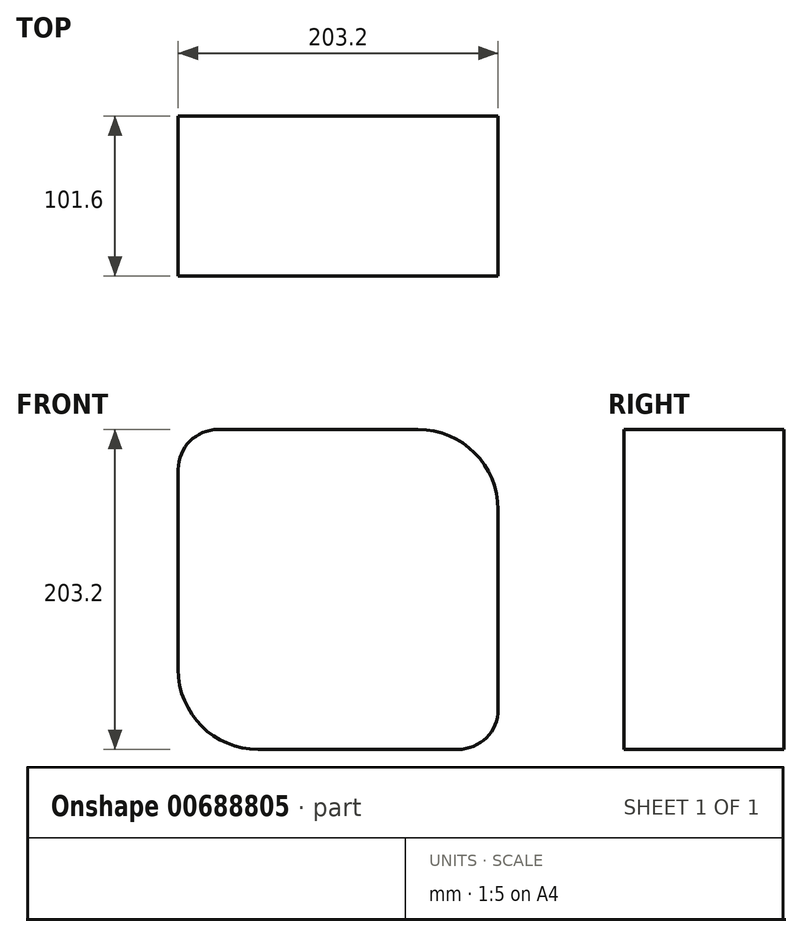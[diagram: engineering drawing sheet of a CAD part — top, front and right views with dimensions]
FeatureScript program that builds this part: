
annotation { "Feature Type Name" : "Feature", "Feature Type Description" : "" }
export const myFeature = defineFeature(function(context is Context, id is Id, definition is map)
    precondition{}
    {
        {
            var Q0;
            Q0=qCreatedBy(makeId("Front.planeOp"),FACE);
            var sketch = newSketch(context, id + "F0", { "sketchPlane" : qUnion([Q0])});
            skLineSegment(sketch, "E0.bottom", {"start": v(-76.2, 101.6) * mm, "end": v(50.8, 101.6) * mm});
            skLineSegment(sketch, "E0.top", {"start": v(-50.8, -101.6) * mm, "end": v(76.2, -101.6) * mm});
            skLineSegment(sketch, "E1", {"start": v(-101.6, 76.2) * mm, "end": v(-101.6, -50.8) * mm});
            skLineSegment(sketch, "E2", {"start": v(101.6, 50.8) * mm, "end": v(101.6, -76.2) * mm});
            skPoint(sketch, "E3.visualSharp", {"position": v(-101.6, 101.6) * mm});
            skArc(sketch, "E3.filletArc", {"start": v(-76.2, 101.6) * mm, "mid": v(-94.16, 94.16) * mm, "end": v(-101.6, 76.2) * mm});
            skPoint(sketch, "E4.visualSharp", {"position": v(101.6, -101.6) * mm});
            skArc(sketch, "E4.filletArc", {"start": v(76.2, -101.6) * mm, "mid": v(94.16, -94.16) * mm, "end": v(101.6, -76.2) * mm});
            skPoint(sketch, "E5.visualSharp", {"position": v(101.6, 101.6) * mm});
            skArc(sketch, "E5.filletArc", {"start": v(101.6, 50.8) * mm, "mid": v(86.72, 86.72) * mm, "end": v(50.8, 101.6) * mm});
            skPoint(sketch, "E6.visualSharp", {"position": v(-101.6, -101.6) * mm});
            skArc(sketch, "E6.filletArc", {"start": v(-101.6, -50.8) * mm, "mid": v(-86.72, -86.72) * mm, "end": v(-50.8, -101.6) * mm});
            skSolve(sketch);
        }
        {
            var Q0;
            Q0 = qSketchRegion(id + "F0", true);
            var Q1;
            Q1=makeQuery(id+"F0.imprint","IMPRINT",FACE,{"disambiguationData":[TD([[makeQuery(id+"F0.imprint","IMPRINT",EDGE,{"derivedFrom":sQuery(id+"F0.wireOp",EDGE,"E0.bottom")}),-1.0]])]});
            extrude(context, id + "F1", {"entities" : qUnion([Q0, Q1]), "depth" : 101.6 * mm, "offsetDistance" : 25.4 * mm});
        }
    });
